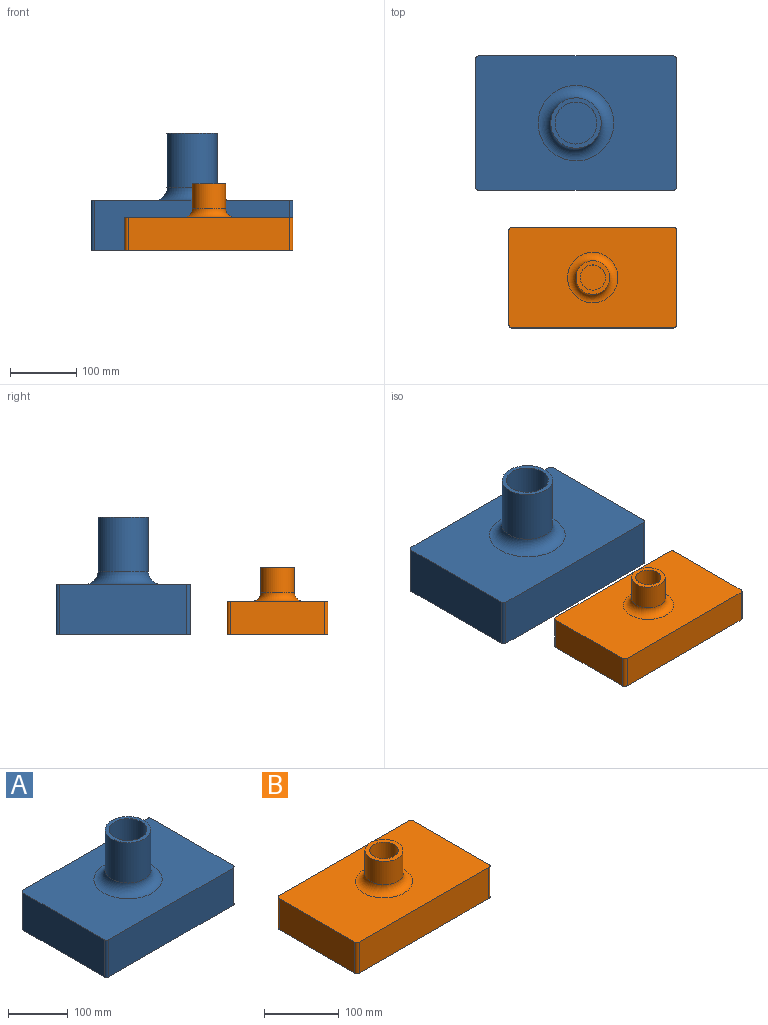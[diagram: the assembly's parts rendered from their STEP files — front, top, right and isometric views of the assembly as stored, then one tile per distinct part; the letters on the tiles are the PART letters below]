
ASSEMBLY  parts=2 mates=2
PART A: 15 faces, bbox 304.8x203.2x177.8 mm
  f0: plane 193.04x76.2mm, normal (1,0,0), area 14709.6mm2, adj f4,f5,f11,f14
  f1: plane 294.64x76.2mm, normal (0,1,0), area 22451.6mm2, adj f4,f5,f11,f12
  f2: plane 193.04x76.2mm, normal (-1,0,0), area 14709.6mm2, adj f4,f5,f12,f13
  f3: plane 294.64x76.2mm, normal (0,-1,0), area 22451.6mm2, adj f4,f5,f13,f14
  f4: plane 304.8x203.2mm, normal (0,0,1), area 51652.4mm2, adj f0,f1,f2,f3,f8,f11,f12,f13
  f5: plane 304.8x203.2mm, normal (0,0,-1), area 61913.2mm2, adj f0,f1,f2,f3,f11,f12,f13,f14
  f6: cylinder r=38.1mm len=82.55mm, axis (0,0,-1), area 19761.6mm2, adj f7,f8
  f7: plane 76.2x76.2mm, normal (0,0,1), area 1393.4mm2, adj f6,f10
  f8: torus R=57.15mm, axis (0,0,1), area 8464.9mm2, adj f4,f6
  f9: plane 63.5x63.5mm, normal (0,0,1), area 3166.9mm2, adj f10
  f10: cylinder r=31.75mm len=101.6mm, axis (0,0,1), area 20268.3mm2, adj f7,f9
  f11: cylinder r=5.08mm len=76.2mm, axis (0,0,1), area 608mm2, adj f0,f1,f4,f5
  f12: cylinder r=5.08mm len=76.2mm, axis (0,0,-1), area 608mm2, adj f1,f2,f4,f5
  f13: cylinder r=5.08mm len=76.2mm, axis (0,0,1), area 608mm2, adj f2,f3,f4,f5
  f14: cylinder r=5.08mm len=76.2mm, axis (0,0,-1), area 608mm2, adj f0,f3,f4,f5
PART B: 15 faces, bbox 254x152.4x101.6 mm
  f0: plane 142.24x50.8mm, normal (1,0,0), area 7225.8mm2, adj f4,f5,f11,f14
  f1: plane 243.84x50.8mm, normal (0,1,0), area 12387.1mm2, adj f4,f5,f11,f12
  f2: plane 142.24x50.8mm, normal (-1,0,0), area 7225.8mm2, adj f4,f5,f12,f13
  f3: plane 243.84x50.8mm, normal (0,-1,0), area 12387.1mm2, adj f4,f5,f13,f14
  f4: plane 254x152.4mm, normal (0,0,1), area 34127.1mm2, adj f0,f1,f2,f3,f8,f11,f12,f13
  f5: plane 254x152.4mm, normal (0,0,-1), area 38687.4mm2, adj f0,f1,f2,f3,f11,f12,f13,f14
  f6: cylinder r=25.4mm len=50.8mm, axis (0,0,-1), area 6080.5mm2, adj f7,f8
  f7: plane 50.8x50.8mm, normal (0,0,1), area 886.7mm2, adj f6,f10
  f8: torus R=38.1mm, axis (0,0,1), area 3762.2mm2, adj f4,f6
  f9: plane 38.1x38.1mm, normal (0,0,1), area 1140.1mm2, adj f10
  f10: cylinder r=19.05mm len=50.8mm, axis (0,0,1), area 6080.5mm2, adj f7,f9
  f11: cylinder r=5.08mm len=50.8mm, axis (0,0,1), area 405.4mm2, adj f0,f1,f4,f5
  f12: cylinder r=5.08mm len=50.8mm, axis (0,0,-1), area 405.4mm2, adj f1,f2,f4,f5
  f13: cylinder r=5.08mm len=50.8mm, axis (0,0,1), area 405.4mm2, adj f2,f3,f4,f5
  f14: cylinder r=5.08mm len=50.8mm, axis (0,0,-1), area 405.4mm2, adj f0,f3,f4,f5
PLACE A t=(-252.02,312.6,75.21)mm
PLACE B t=(-226.62,79.01,75.21)mm fixed
MATE planar A.f0 <-> B.f0  axis (1,0,0) through (-99.62,312.6,113.31)mm
MATE planar B.f5 <-> A.f10  axis (0,0,-1) through (-99.62,79.01,75.21)mm
